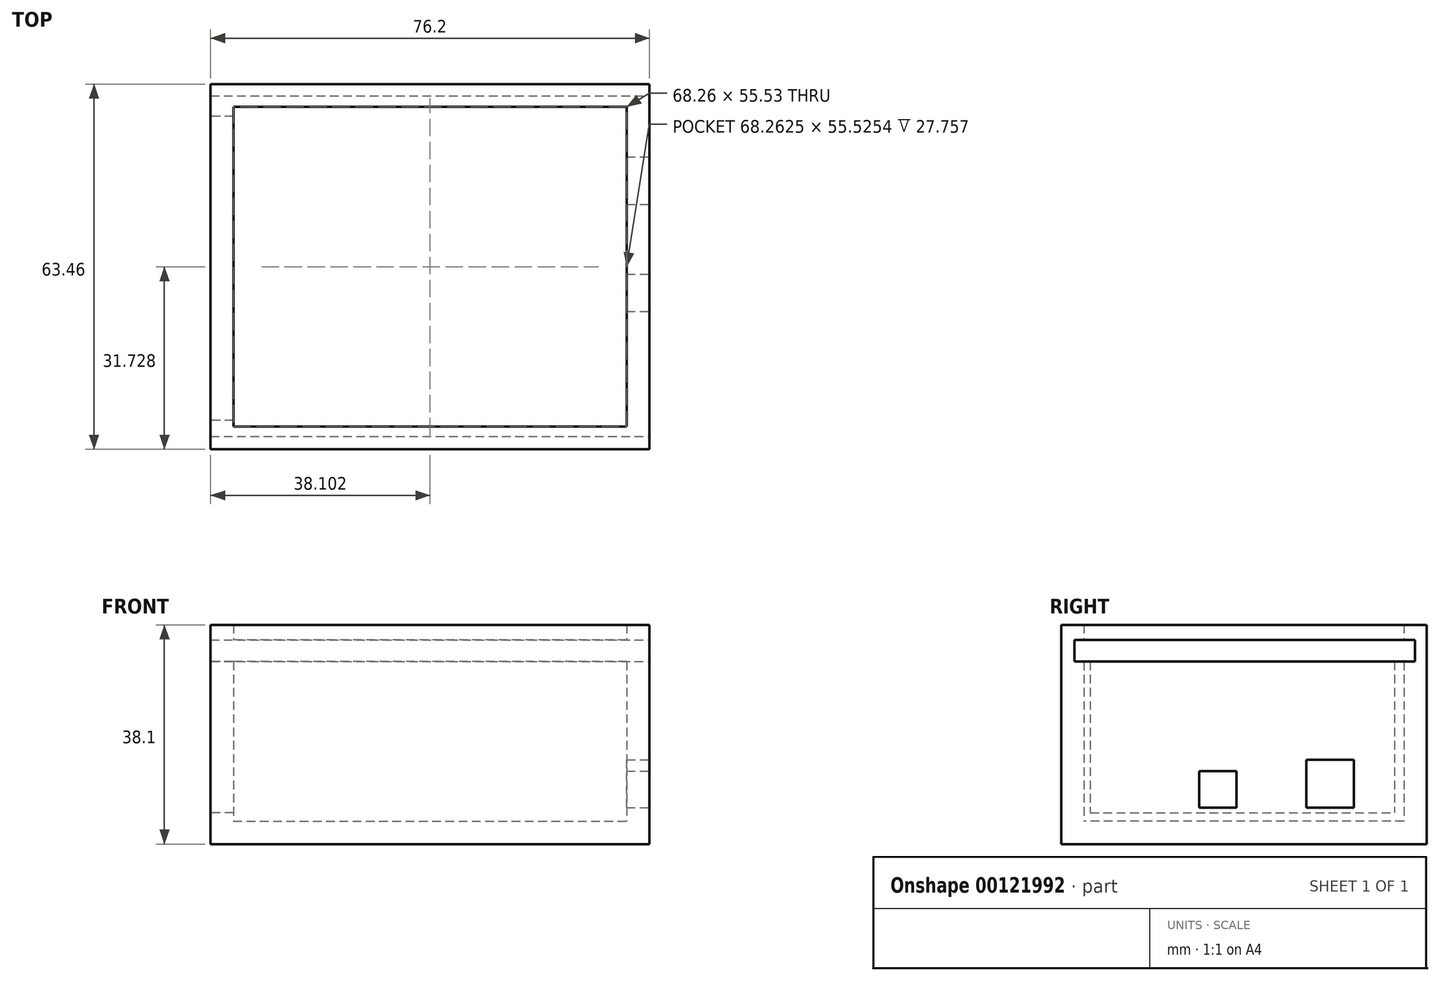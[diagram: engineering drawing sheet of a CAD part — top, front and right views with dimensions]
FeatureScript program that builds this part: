
annotation { "Feature Type Name" : "Feature", "Feature Type Description" : "" }
export const myFeature = defineFeature(function(context is Context, id is Id, definition is map)
    precondition{}
    {
        {
            var Q0;
            Q0=qCreatedBy(makeId("Top.planeOp"),FACE);
            var sketch = newSketch(context, id + "F0", { "sketchPlane" : qUnion([Q0])});
            skLineSegment(sketch, "E0.bottom", {"start": v(-31.27, 30.63) * mm, "end": v(44.93, 30.63) * mm});
            skLineSegment(sketch, "E0.top", {"start": v(-31.27, -32.83) * mm, "end": v(44.93, -32.83) * mm});
            skLineSegment(sketch, "E0.left", {"start": v(-31.27, 30.63) * mm, "end": v(-31.27, -32.83) * mm});
            skLineSegment(sketch, "E0.right", {"start": v(44.93, 30.63) * mm, "end": v(44.93, -32.83) * mm});
            skSolve(sketch);
        }
        {
            var Q0;
            Q0=makeQuery(id+"F0.imprint","IMPRINT",FACE,{"disambiguationData":[TD([[makeQuery(id+"F0.imprint","IMPRINT",EDGE,{"derivedFrom":sQuery(id+"F0.wireOp",EDGE,"E0.bottom")}),-1.0]])]});
            extrude(context, id + "F1", {"entities" : qUnion([Q0]), "depth" : 38.1 * mm});
        }
        {
            var Q0;
            Q0=makeQuery(id+"F1.opExtrude","CAP_FACE",FACE,{"disambiguationData":[OSD([sQuery(id+"F0.wireOp",EDGE,"E0.bottom"),sQuery(id+"F0.wireOp",EDGE,"E0.top"),sQuery(id+"F0.wireOp",EDGE,"E0.left"),sQuery(id+"F0.wireOp",EDGE,"E0.right")])],"isStart":false});
            shell(context, id + "F2", {"entities" : qUnion([Q0]), "thickness" : 3.97 * mm});
        }
        {
            var Q0;
            Q0=makeQuery(id+"F1.opExtrude","SWEPT_FACE",FACE,{"disambiguationData":[OSD([sQuery(id+"F0.wireOp",EDGE,"E0.right")])]});
            var sketch = newSketch(context, id + "F3", { "sketchPlane" : qUnion([Q0])});
            skLineSegment(sketch, "E1.bottom", {"start": v(-30.57, 35.5) * mm, "end": v(28.59, 35.5) * mm});
            skLineSegment(sketch, "E1.top", {"start": v(-30.57, 31.73) * mm, "end": v(28.59, 31.73) * mm});
            skLineSegment(sketch, "E1.left", {"start": v(-30.57, 35.5) * mm, "end": v(-30.57, 31.73) * mm});
            skLineSegment(sketch, "E1.right", {"start": v(28.59, 35.5) * mm, "end": v(28.59, 31.73) * mm});
            skSolve(sketch);
        }
        {
            var Q0;
            Q0 = qSketchRegion(id + "F3", true);
            extrude(context, id + "F4", {"entities" : qUnion([Q0]), "operationType" : NewBodyOperationType.REMOVE, "oppositeDirection" : true, "depth" : 84.45 * mm});
        }
        {
            var Q0;
            Q0=makeQuery(id+"F1.opExtrude","SWEPT_FACE",FACE,{"disambiguationData":[OSD([sQuery(id+"F0.wireOp",EDGE,"E0.right")])]});
            var sketch = newSketch(context, id + "F5", { "sketchPlane" : qUnion([Q0])});
            skLineSegment(sketch, "E2.bottom", {"start": v(18, 6.35) * mm, "end": v(9.74, 6.35) * mm});
            skLineSegment(sketch, "E2.top", {"start": v(18, 14.61) * mm, "end": v(9.74, 14.61) * mm});
            skLineSegment(sketch, "E2.left", {"start": v(18, 6.35) * mm, "end": v(18, 14.61) * mm});
            skLineSegment(sketch, "E2.right", {"start": v(9.74, 6.35) * mm, "end": v(9.74, 14.61) * mm});
            skLineSegment(sketch, "E3.bottom", {"start": v(-2.38, 6.35) * mm, "end": v(-8.9, 6.35) * mm});
            skLineSegment(sketch, "E3.top", {"start": v(-2.38, 12.7) * mm, "end": v(-8.9, 12.7) * mm});
            skLineSegment(sketch, "E3.left", {"start": v(-2.38, 6.35) * mm, "end": v(-2.38, 12.7) * mm});
            skLineSegment(sketch, "E3.right", {"start": v(-8.9, 6.35) * mm, "end": v(-8.9, 12.7) * mm});
            skSolve(sketch);
        }
        {
            var Q0;
            Q0=makeQuery(id+"F5.imprint","IMPRINT",FACE,{"disambiguationData":[TD([[makeQuery(id+"F5.imprint","IMPRINT",EDGE,{"derivedFrom":sQuery(id+"F5.wireOp",EDGE,"E2.bottom")}),-1.0]])]});
            var Q1;
            Q1=makeQuery(id+"F5.imprint","IMPRINT",FACE,{"disambiguationData":[TD([[makeQuery(id+"F5.imprint","IMPRINT",EDGE,{"derivedFrom":sQuery(id+"F5.wireOp",EDGE,"E3.bottom")}),-1.0]])]});
            extrude(context, id + "F6", {"entities" : qUnion([Q0, Q1]), "operationType" : NewBodyOperationType.REMOVE, "oppositeDirection" : true, "depth" : 6.35 * mm});
        }
        {
            var Q0;
            Q0=makeQuery(id+"F6.boolean.opBoolean","MERGE",FACE,{"derivedFrom":[makeQuery(id+"F2.opShell","OFFSET_FACE",FACE,{"disambiguationData":[OSD([sQuery(id+"F0.wireOp",EDGE,"E0.bottom"),sQuery(id+"F0.wireOp",EDGE,"E0.top"),sQuery(id+"F0.wireOp",EDGE,"E0.left"),sQuery(id+"F0.wireOp",EDGE,"E0.right")])]}),makeQuery(id+"F6.opExtrude","SWEPT_FACE",FACE,{"disambiguationData":[OSD([sQuery(id+"F5.wireOp",EDGE,"E2.bottom")])]}),makeQuery(id+"F6.opExtrude","SWEPT_FACE",FACE,{"disambiguationData":[OSD([sQuery(id+"F5.wireOp",EDGE,"E3.bottom")])]})]});
            var sketch = newSketch(context, id + "F7", { "sketchPlane" : qUnion([Q0])});
            skSolve(sketch);
        }
        {
            var Q0;
            Q0=makeQuery(id+"F1.opExtrude","SWEPT_FACE",FACE,{"disambiguationData":[OSD([sQuery(id+"F0.wireOp",EDGE,"E0.left")])]});
            var sketch = newSketch(context, id + "F8", { "sketchPlane" : qUnion([Q0])});
            skLineSegment(sketch, "E4.bottom", {"start": v(-25.04, 5.42) * mm, "end": v(27.8, 5.42) * mm});
            skLineSegment(sketch, "E4.top", {"start": v(-25.04, 31.73) * mm, "end": v(27.8, 31.73) * mm});
            skLineSegment(sketch, "E4.left", {"start": v(-25.04, 5.42) * mm, "end": v(-25.04, 31.73) * mm});
            skLineSegment(sketch, "E4.right", {"start": v(27.8, 5.42) * mm, "end": v(27.8, 31.73) * mm});
            skSolve(sketch);
        }
        {
            var Q0;
            Q0 = qSketchRegion(id + "F8", true);
            extrude(context, id + "F9", {"entities" : qUnion([Q0]), "operationType" : NewBodyOperationType.REMOVE, "oppositeDirection" : true, "depth" : 6.35 * mm});
        }
    });
